# Revit family: HC_Storage Tank_MEPcontent_De Dietrich Thermique_DHW_BPB
name_source: partatom
category: Mechanical Equipment
revit_build: Autodesk Revit 2018 (Build: 20170223_1515(x64)
units: mm (PartAtom-declared; Revit-internal decimal feet)

## family parameters
Always vertical = Yes
Cut with Voids When Loaded = No
OmniClass Number = 23.75.10.34.11
OmniClass Title = Energy Storage Tanks
Part Type = Normal
Room Calculation Point = No
Round Connector Dimension = Use Diameter
Shared = No
Work Plane-Based = No

## types (5) — shared parameters
Article Description = “Performance”, independent calorifiers
Black = Color RGB 020-020-020
Content Supplier URL = www.MEPcontent.com
Custom = No
Description = “Performance”, independent calorifiers
Domestic Cold Water Diameter = 25 mm  [stored 0.082021 ft]
Domestic Hot Water Diameter 1 = 25 mm  [stored 0.082021 ft]
Domestic Hot Water Diameter 2 = 19 mm  [stored 0.062336 ft]
EMCS Version = 2.0
ETIM Article Class = EC010184
Family Version = 11.14
Grey = Color RAL 9006
Hydronic Return Diameter = 25 mm  [stored 0.082021 ft]
Hydronic Supply Diameter = 25 mm  [stored 0.082021 ft]
IFCExportAs = IfcTankType
IFCExportType = NOTDEFINED
MEPcontent Class = STORAGE_TANK_HC
Manufacturer = De Dietrich Thermique
Manufacturer URL = http://www.dedietrich-thermique.fr
Product Line = De Dietrich Thermique
Revit Version = 2018
Service Area = Color RGB 218-227-224
URL = www.stabiplan.com
Use Nominal Diameter = Yes
White = Color RAL 9016
zero-valued in all types: Offset

## per-type parameters (varying)
| type | A | B | C | Connection Length | D | E | F | G | GTIN | Logo Void | Manufacturer Art. No. | Radius | Thermometer Void | Volume |
| BPB 150 | 70 mm | 282 mm | 612 mm | 350 mm | 692 mm | 844 mm | 655 mm  [stored 2.14895 ft] | 964 mm | 3661238549555 | 331 mm | 100018093 | 328 mm | 330 mm | 150.0 L |
| BPB 200 | 70 mm | 282 mm | 747 mm | 350 mm | 910 mm | 1114 mm | 655 mm  [stored 2.14895 ft] | 1234 mm | 3661238551084 | 331 mm | 100018094 | 328 mm | 330 mm | 200.0 L |
| BPB 300 | 70 mm | 282 mm | 972 mm | 350 mm | 1262 mm | 1634 mm | 655 mm  [stored 2.14895 ft] | 1754 mm | 3661238551091 | 331 mm | 100018095 | 328 mm | 330 mm | 300.0 L |
| BPB 400 | 66 mm | 282 mm | 972 mm | 400 mm  [stored 1.31234 ft] | 1220 mm | 1509 mm | 755 mm | 1642 mm | 3661238551107 | 381 mm  [stored 1.25 ft] | 100018096 | 378 mm | 380 mm | 395.0 L |
| BPB 500 | 71 mm | 283 mm | 1152 mm | 425 mm | 1348 mm | 1618 mm | 805 mm | 1760 mm | 3661238551114 | 406 mm | 100018097 | 403 mm | 405 mm | 500.0 L |

note: column(s) folded — value = type name in every type: Article Type, Model

note: [stored X ft] marks values corroborated as IEEE doubles in the binary element streams (Revit-internal decimal feet)

## geometry (parser evidence)
native form markers: Sweep x3
no freeform markers — native parametric forms only
